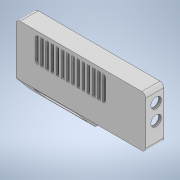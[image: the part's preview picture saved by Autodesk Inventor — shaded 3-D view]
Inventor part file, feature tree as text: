
AUTODESK INVENTOR PART (.ipt)
format: ipt  version: 2021 (Build 250183000, 183)  size: 527,872 bytes
history: native  units: mm
features: sketch x21, extrude x20, chamfer x5, fillet x4, hole x1
ambient origin geometry x8: Origin, YZ Plane, XZ Plane, XY Plane, X Axis, Y Axis, Z Axis, Center Point
bodies: Solid1 (feature_tree)
feature tree (51):
  extrude  "Extrusion1"  Depth=100.0mm
  extrude  "Extrusion3"  Depth=50.0mm
  extrude  "Extrusion4"  Depth=2.0mm
  extrude  "Extrusion12"  Depth=3.0mm TaperAngle=0.0deg
  extrude  "Extrusion13"  Depth=3.0mm TaperAngle=0.0deg
  fillet  "Fillet3"  Radius=2.0mm
  extrude  "Extrusion15"  Depth=2.0mm
  extrude  "Extrusion20"  Depth=1.2mm
  extrude  "Extrusion21"  Depth=12.0mm TaperAngle=0.0deg
  extrude  "Extrusion22"  Depth=2.0mm
  extrude  "Extrusion23"  Depth=3.0mm
  extrude  "Extrusion26"  Depth=4.4mm TaperAngle=0.0deg
  hole  "Hole2"  [1 undecoded]
  chamfer  "Chamfer3"  Distance=12.0mm
  chamfer  "Chamfer4"  Distance=12.0mm
  chamfer  "Chamfer5"  Distance=2.0mm
  chamfer  "Chamfer6"  Distance=8.0mm
  chamfer  "Chamfer7"  Distance=2.0mm
  extrude  "Extrusion27"  Depth=3.0mm
  fillet  "Fillet4"  Radius=3.0mm
  extrude  "Extrusion28"  Depth=3.0mm
  extrude  "Extrusion29"  Depth=0.5mm
  extrude  "Extrusion30"  Depth=0.5mm
  fillet  "Fillet5"  Radius=15.0mm
  extrude  "Extrusion34"  Depth=3.0mm
  extrude  "Extrusion35"  Depth=3.0mm
  extrude  "Extrusion36"  Depth=0.5mm
  extrude  "Extrusion37"  Depth=0.5mm
  fillet  "Fillet6"  Radius=4.8mm
  extrude  "Extrusion38"  Depth=0.5mm
  sketch  "Sketch1"  dims[d0=52.0mm d1=100.0mm]
  sketch  "Sketch4"  dims[d2=26.0mm d3=50.0mm]
  sketch  "Sketch5"  dims[d4=2.0mm d5=0.0mm d35=12.5mm]
  sketch  "Sketch13"  dims[d36=63.1mm d37=3.0mm d38=0.0mm]
  sketch  "Sketch14"  dims[d39=50.673mm d40=3.0mm d41=0.0mm d79=2.0mm]
  sketch  "Sketch16"  dims[d80=2.0mm d81=2.0mm]
  sketch  "Sketch21"  dims[d82=1.2mm d83=44.0mm]
  sketch  "Sketch22"  dims[d84=59.0mm d85=12.0mm d86=0.0mm]
  sketch  "Sketch23"  dims[d87=2.0mm d88=12.6mm]
  sketch  "Sketch24"  dims[d89=12.0mm d90=0.0mm d91=3.0mm]
  sketch  "Sketch27"  dims[d95=33.8mm d96=4.4mm d97=0.0mm]
  sketch  "Sketch28"  dims[d117=2.0mm d118=2.0mm d119=12.0mm d120=0.0mm d121=12.0mm d122=0.0mm]
  sketch  "Sketch29"  dims[d123=70.0mm]
  sketch  "Sketch30"  dims[d124=89.0mm]
  sketch  "Sketch31"  dims[d125=8.0mm]
  sketch  "Sketch32"  dims[d126=8.0mm d127=2.0mm d128=0.0mm]
  sketch  "Sketch36"  dims[d129=8.0mm]
  sketch  "Sketch37"  dims[d130=10.0mm]
  sketch  "Sketch38"  dims[d131=12.0mm]
  sketch  "Sketch39"  dims[d132=8.0mm]
  sketch  "Sketch40"  dims[d133=8.0mm d134=8.0mm d135=2.0mm d136=0.0mm d144=3.0mm d145=3.0mm d146=3.0mm d147=50.0mm d148=97.0mm d149=15.0mm d150=3.0mm d151=3.0mm d152=97.0mm d153=49.0mm d154=4.8mm d155=4.8mm d156=4.8mm d157=4.8mm d158=4.8mm d159=5.0mm d160=0.0mm d161=2.0mm d162=6.0mm d163=4.0mm d164=2.0mm d165=90.0deg d166=4.0mm d167=20.594885mm d168=2.0mm d169=2.0mm d170=45.0deg d171=1.0mm d172=2.0mm d173=45.0deg d174=2.0mm d175=2.0mm d176=45.0deg d177=2.0mm d178=2.0mm d179=45.0deg d180=0.8mm d181=2.0mm d182=45.0deg d184=68.0mm d189=2.0mm d190=0.0mm d191=2.0mm d192=2.0mm d193=24.0mm d194=2.0mm d195=0.0mm d196=36.5mm d197=46.5mm d198=3.5mm d199=2.0mm d200=0.0mm d201=12.5mm d202=23.0mm d203=3.5mm d204=2.0mm d205=0.0mm d206=1.0mm d217=7.6mm d218=10.0mm d219=46.4mm d220=20.0mm d221=0.0mm d222=22.68928mm d223=67.0mm d224=0.0mm d225=1.2mm d226=0.0mm d227=1.2mm d228=0.0mm d229=3.0mm d230=12.3mm d231=33.2mm d232=1.0mm d233=10.0mm d234=1.2mm d235=0.0mm d67=0.5mm d68=0.872665mm d69=0.5mm d70=0.872665mm d71=0.5mm d72=0.872665mm d73=0.5mm d74=0.872665mm d75=0.872665mm d76=0.5mm d77=0.872665mm d208=0.5mm d209=0.872665mm d210=0.5mm d211=0.872665mm]
note: 1 required parameter value undecoded (feature->parameter linkage not recoverable at this tier; creation-order binding heuristic only, values carry confidence <= 0.55)
